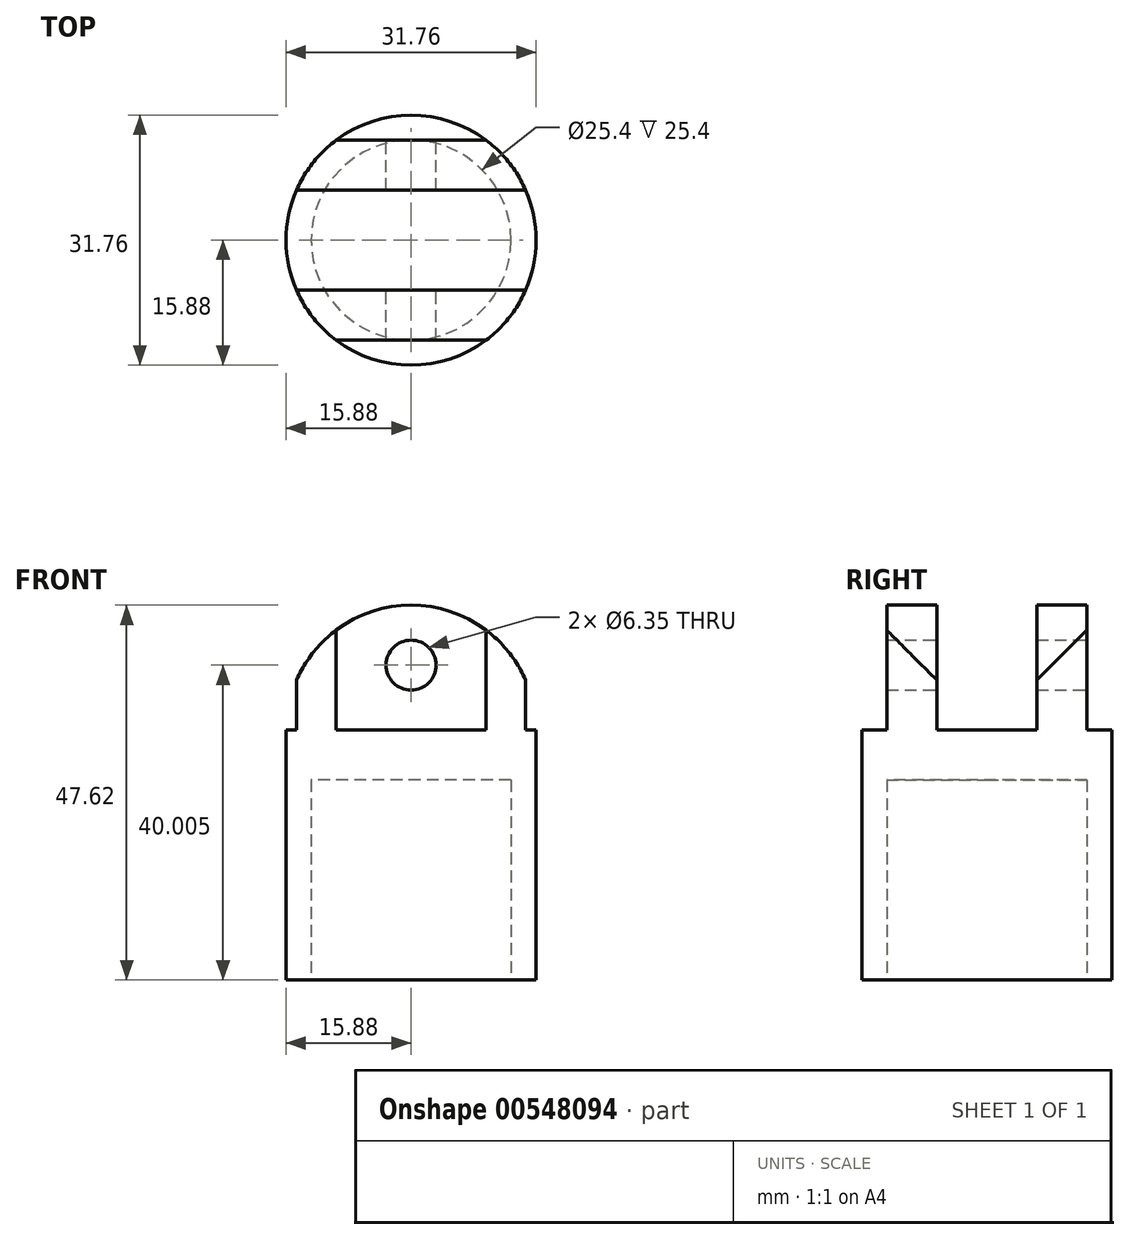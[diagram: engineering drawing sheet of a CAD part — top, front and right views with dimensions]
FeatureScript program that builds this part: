
annotation { "Feature Type Name" : "Feature", "Feature Type Description" : "" }
export const myFeature = defineFeature(function(context is Context, id is Id, definition is map)
    precondition{}
    {
        {
            var Q0;
            Q0=qCreatedBy(makeId("Top.planeOp"),FACE);
            var sketch = newSketch(context, id + "F0", { "sketchPlane" : qUnion([Q0])});
            skCircle(sketch, "E0", {"center": v(0, 0) * mm, "radius": 15.88 * mm});
            skCircle(sketch, "E1", {"center": v(0, 0) * mm, "radius": 12.7 * mm});
            skSolve(sketch);
        }
        {
            var Q0;
            Q0=makeQuery(id+"F0.imprint","IMPRINT",FACE,{"disambiguationData":[TD([[makeQuery(id+"F0.imprint","IMPRINT",EDGE,{"derivedFrom":sQuery(id+"F0.wireOp",EDGE,"E0")}),1.0]])]});
            extrude(context, id + "F1", {"entities" : qUnion([Q0]), "depth" : 25.4 * mm, "offsetDistance" : 25.4 * mm});
        }
        {
            var Q0;
            Q0=makeQuery(id+"F1.opExtrude","CAP_FACE",FACE,{"disambiguationData":[OSD([sQuery(id+"F0.wireOp",EDGE,"E0"),sQuery(id+"F0.wireOp",EDGE,"E1")])],"isStart":false});
            var sketch = newSketch(context, id + "F2", { "sketchPlane" : qUnion([Q0])});
            skCircle(sketch, "E2", {"center": v(0, 0) * mm, "radius": 15.88 * mm});
            skSolve(sketch);
        }
        {
            var Q0;
            Q0 = qSketchRegion(id + "F2", true);
            extrude(context, id + "F3", {"entities" : qUnion([Q0]), "operationType" : NewBodyOperationType.ADD, "depth" : 6.35 * mm, "offsetDistance" : 25.4 * mm});
        }
        {
            var Q0;
            Q0=qCreatedBy(makeId("Front.planeOp"),FACE);
            var sketch = newSketch(context, id + "F4", { "sketchPlane" : qUnion([Q0])});
            skLineSegment(sketch, "E3.bottom", {"start": v(-15.88, 31.75) * mm, "end": v(15.88, 31.75) * mm});
            skLineSegment(sketch, "E3.top", {"start": v(-15.88, 25.4) * mm, "end": v(15.88, 25.4) * mm});
            skLineSegment(sketch, "E3.left", {"start": v(-15.88, 31.75) * mm, "end": v(-15.88, 25.4) * mm});
            skLineSegment(sketch, "E3.right", {"start": v(15.88, 31.75) * mm, "end": v(15.88, 25.4) * mm});
            skArc(sketch, "E4", {"start": v(15.88, 31.75) * mm, "mid": v(0, 47.62) * mm, "end": v(-15.88, 31.75) * mm});
            skCircle(sketch, "E5", {"center": v(0, 40) * mm, "radius": 3.18 * mm});
            skSolve(sketch);
        }
        {
            var Q0;
            Q0=makeQuery(id+"F4.imprint","IMPRINT",FACE,{"disambiguationData":[TD([[makeQuery(id+"F4.imprint","IMPRINT",EDGE,{"derivedFrom":sQuery(id+"F4.wireOp",EDGE,"E3.bottom")}),1.0]])]});
            extrude(context, id + "F5", {"entities" : qUnion([Q0]), "operationType" : NewBodyOperationType.ADD, "depth" : 12.7 * mm, "offsetDistance" : 25.4 * mm, "hasSecondDirection" : true, "secondDirectionOppositeDirection" : true, "secondDirectionDepth" : 12.7 * mm});
        }
        {
            var Q0;
            Q0=qCreatedBy(makeId("Front.planeOp"),FACE);
            var sketch = newSketch(context, id + "F6", { "sketchPlane" : qUnion([Q0])});
            skLineSegment(sketch, "E6.bottom", {"start": v(-15.88, 0) * mm, "end": v(-37.34, 0) * mm});
            skLineSegment(sketch, "E6.top", {"start": v(-15.88, 60.37) * mm, "end": v(-37.34, 60.37) * mm});
            skLineSegment(sketch, "E6.left", {"start": v(-15.88, 0) * mm, "end": v(-15.88, 60.37) * mm});
            skLineSegment(sketch, "E6.right", {"start": v(-37.34, 0) * mm, "end": v(-37.34, 60.37) * mm});
            skLineSegment(sketch, "E7", {"start": v(0, -10.16) * mm, "end": v(0, 70.36) * mm});
            skSolve(sketch);
        }
        {
            var Q0;
            Q0=makeQuery(id+"F6.imprint","IMPRINT",FACE,{"disambiguationData":[TD([[makeQuery(id+"F6.imprint","IMPRINT",EDGE,{"derivedFrom":sQuery(id+"F6.wireOp",EDGE,"E6.bottom")}),-1.0]])]});
            var Q1;
            Q1=sQuery(id+"F6.wireOp",EDGE,"E7");
            revolve(context, id + "F7", {"operationType" : NewBodyOperationType.REMOVE, "entities" : qUnion([Q0]), "axis" : qUnion([Q1]), "revolveType" : RevolveType.FULL, "oppositeDirection" : true});
        }
        {
            var Q0;
            Q0=qCreatedBy(makeId("Right.planeOp"),FACE);
            var sketch = newSketch(context, id + "F8", { "sketchPlane" : qUnion([Q0])});
            skLineSegment(sketch, "E8.bottom", {"start": v(6.35, 59.7) * mm, "end": v(-6.35, 59.7) * mm});
            skLineSegment(sketch, "E8.top", {"start": v(6.35, 31.75) * mm, "end": v(-6.35, 31.75) * mm});
            skLineSegment(sketch, "E8.left", {"start": v(6.35, 59.7) * mm, "end": v(6.35, 31.75) * mm});
            skLineSegment(sketch, "E8.right", {"start": v(-6.35, 59.7) * mm, "end": v(-6.35, 31.75) * mm});
            skSolve(sketch);
        }
        {
            var Q0;
            Q0 = qSketchRegion(id + "F8", true);
            extrude(context, id + "F9", {"entities" : qUnion([Q0]), "operationType" : NewBodyOperationType.REMOVE, "oppositeDirection" : true, "depth" : 25.4 * mm, "offsetDistance" : 25.4 * mm, "hasSecondDirection" : true, "secondDirectionOppositeDirection" : false, "secondDirectionDepth" : 25.4 * mm});
        }
    });
